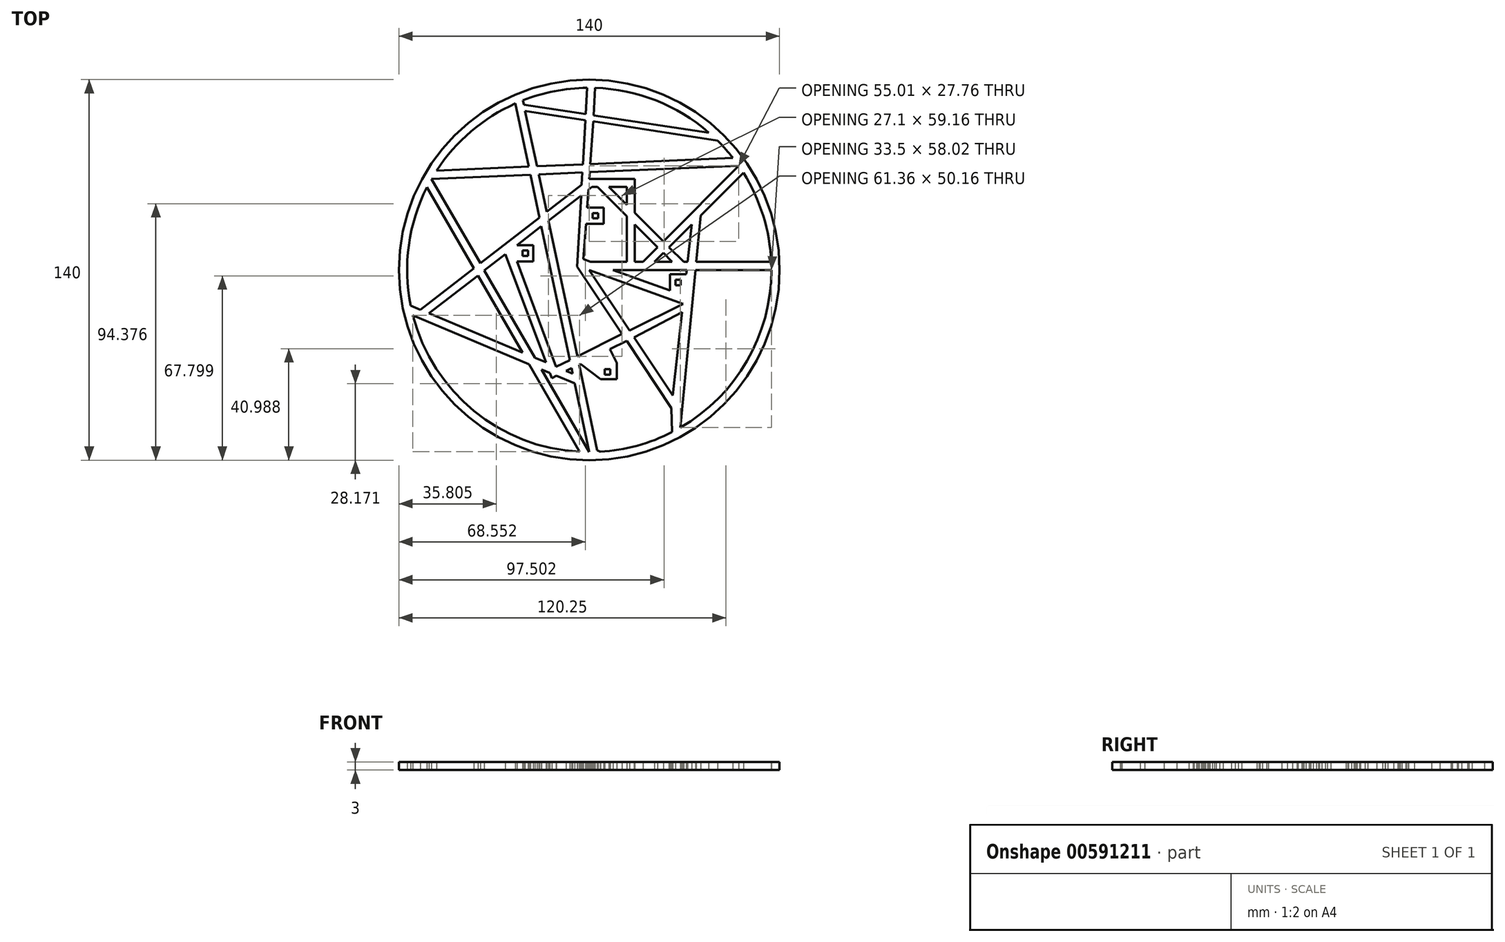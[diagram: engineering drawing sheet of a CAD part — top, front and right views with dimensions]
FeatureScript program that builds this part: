
annotation { "Feature Type Name" : "Feature", "Feature Type Description" : "" }
export const myFeature = defineFeature(function(context is Context, id is Id, definition is map)
    precondition{}
    {
        {
            var Q0;
            Q0=qCreatedBy(makeId("Top.planeOp"),FACE);
            var sketch = newSketch(context, id + "F0", { "sketchPlane" : qUnion([Q0])});
            skCircle(sketch, "E0", {"center": v(0, 0) * mm, "radius": 70 * mm});
            skArc(sketch, "E1.0", {"start": v(66.93, 3) * mm, "mid": v(63.94, 20.02) * mm, "end": v(56.7, 35.7) * mm});
            skLineSegment(sketch, "E2", {"start": v(67, 0) * mm, "end": v(39.1, 0) * mm});
            skLineSegment(sketch, "E3", {"start": v(30.5, 3) * mm, "end": v(27.25, 6.25) * mm});
            skLineSegment(sketch, "E4", {"start": v(0, 33.5) * mm, "end": v(16.75, 33.5) * mm});
            skPoint(sketch, "E4.endSnap0", {"position": v(16.75, 16.75) * mm});
            skLineSegment(sketch, "E5", {"start": v(16.75, 33.5) * mm, "end": v(16.75, 21) * mm});
            skLineSegment(sketch, "E6", {"start": v(19.75, 3) * mm, "end": v(25.12, 8.37) * mm});
            skLineSegment(sketch, "E7", {"start": v(55, 38.26) * mm, "end": v(0.18, 35.95) * mm});
            skPoint(sketch, "E7.endSnap0", {"position": v(8.38, 33.5) * mm});
            skLineSegment(sketch, "E8", {"start": v(-58.02, 33.5) * mm, "end": v(-40.1, 2.44) * mm});
            skLineSegment(sketch, "E9", {"start": v(0, -67) * mm, "end": v(-5.37, -41.72) * mm});
            skLineSegment(sketch, "E10", {"start": v(-24.05, 60.75) * mm, "end": v(-1.35, 57.34) * mm});
            skPoint(sketch, "E11.endSnap0", {"position": v(-29.01, -16.75) * mm});
            skLineSegment(sketch, "E12", {"start": v(-62.15, -14.64) * mm, "end": v(-42.49, 0.59) * mm});
            skLineSegment(sketch, "E13.0", {"start": v(-58.97, -15.97) * mm, "end": v(-40.97, -2.03) * mm});
            skLineSegment(sketch, "E14.0", {"start": v(67, 3) * mm, "end": v(39.39, 3) * mm});
            skLineSegment(sketch, "E15.0", {"start": v(-0.82, 67) * mm, "end": v(-1.35, 57.34) * mm});
            skLineSegment(sketch, "E16.0", {"start": v(52.86, 41.17) * mm, "end": v(0.4, 38.96) * mm});
            skLineSegment(sketch, "E16.1", {"start": v(24, 3) * mm, "end": v(27.25, 6.25) * mm});
            skLineSegment(sketch, "E17.0", {"start": v(13.75, 30.5) * mm, "end": v(13.75, 24) * mm});
            skLineSegment(sketch, "E17.1", {"start": v(1.03, 30.5) * mm, "end": v(3, 30.5) * mm});
            skLineSegment(sketch, "E18.0", {"start": v(34.74, 3) * mm, "end": v(29.37, 8.37) * mm});
            skLineSegment(sketch, "E19", {"start": v(-26.63, 3.13) * mm, "end": v(-12.15, -35.62) * mm});
            skLineSegment(sketch, "E20", {"start": v(-12.15, -35.62) * mm, "end": v(-7.19, -33.15) * mm});
            skLineSegment(sketch, "E21", {"start": v(34.46, -12.53) * mm, "end": v(0, 0) * mm});
            skLineSegment(sketch, "E22", {"start": v(30.23, -50.85) * mm, "end": v(13.76, -26.1) * mm});
            skLineSegment(sketch, "E23.0", {"start": v(30.74, -46.2) * mm, "end": v(16.47, -24.76) * mm});
            skLineSegment(sketch, "E24.0", {"start": v(-13.8, -39.78) * mm, "end": v(-12.05, -38.91) * mm});
            skLineSegment(sketch, "E24.1", {"start": v(-30.84, 5.82) * mm, "end": v(-15.95, -34.02) * mm});
            skLineSegment(sketch, "E25.0", {"start": v(29.67, -7.6) * mm, "end": v(8.78, 0) * mm});
            skLineSegment(sketch, "E26.0", {"start": v(-59.7, 30.4) * mm, "end": v(-42.49, 0.59) * mm});
            skLineSegment(sketch, "E27.0", {"start": v(2.93, -66.38) * mm, "end": v(-3.76, -34.86) * mm});
            skLineSegment(sketch, "E28", {"start": v(2.93, -66.38) * mm, "end": v(3.98, -66.88) * mm});
            skLineSegment(sketch, "E29.trimOffspring", {"start": v(0.53, 3) * mm, "end": v(-2.13, 3.97) * mm});
            skLineSegment(sketch, "E30.trimOffspring", {"start": v(13.75, 3) * mm, "end": v(0.53, 3) * mm});
            skPoint(sketch, "E31.orphan", {"position": v(16.75, 0) * mm});
            skLineSegment(sketch, "E32.trimOffspring", {"start": v(19.75, 3) * mm, "end": v(16.75, 3) * mm});
            skPoint(sketch, "E33.orphan", {"position": v(33.5, 0) * mm});
            skLineSegment(sketch, "E34.trimOffspring", {"start": v(30.5, 3) * mm, "end": v(24, 3) * mm});
            skLineSegment(sketch, "E35.trimOffspring", {"start": v(29.37, 8.37) * mm, "end": v(37.7, 16.7) * mm});
            skLineSegment(sketch, "E36.trimOffspring", {"start": v(27.25, 10.5) * mm, "end": v(16.75, 21) * mm});
            skLineSegment(sketch, "E37.trimOffspring", {"start": v(27.25, 10.5) * mm, "end": v(55, 38.26) * mm});
            skLineSegment(sketch, "E38.trimOffspring", {"start": v(25.12, 8.38) * mm, "end": v(16.75, 16.75) * mm});
            skLineSegment(sketch, "E39.trimOffspring", {"start": v(37.7, 16.7) * mm, "end": v(36.18, 3) * mm});
            skLineSegment(sketch, "E40.trimOffspring", {"start": v(41.03, 20.04) * mm, "end": v(39.39, 3) * mm});
            skLineSegment(sketch, "E41.trimOffspring", {"start": v(-5.37, -41.72) * mm, "end": v(-12.05, -38.91) * mm});
            skPoint(sketch, "E42.0.start.orphan", {"position": v(39.06, 29.09) * mm});
            skLineSegment(sketch, "E43.trimOffspring", {"start": v(41.03, 20.04) * mm, "end": v(56.7, 35.7) * mm});
            skLineSegment(sketch, "E44.trimOffspring", {"start": v(35.85, 0) * mm, "end": v(8.78, 0) * mm});
            skLineSegment(sketch, "E45.trimOffspring", {"start": v(35.85, 0) * mm, "end": v(35.67, -1.6) * mm});
            skLineSegment(sketch, "E46.trimOffspring", {"start": v(36.18, 3) * mm, "end": v(34.74, 3) * mm});
            skLineSegment(sketch, "E47.trimOffspring", {"start": v(39.1, 0) * mm, "end": v(33.5, -58.02) * mm});
            skPoint(sketch, "E13.1.start.orphan", {"position": v(34.66, -55.26) * mm});
            skArc(sketch, "E48.trimOffspring", {"start": v(3.98, -66.88) * mm, "mid": v(17.62, -64.64) * mm, "end": v(30.5, -59.66) * mm});
            skLineSegment(sketch, "E49.trimOffspring", {"start": v(-6.13, -38.14) * mm, "end": v(-8.5, -37.15) * mm});
            skLineSegment(sketch, "E50.trimOffspring", {"start": v(-6.13, -38.14) * mm, "end": v(-6.54, -36.18) * mm});
            skLineSegment(sketch, "E51.trimOffspring", {"start": v(16.47, -24.76) * mm, "end": v(34.13, -15.53) * mm});
            skLineSegment(sketch, "E52.trimOffspring", {"start": v(14.81, -22.26) * mm, "end": v(34.46, -12.53) * mm});
            skLineSegment(sketch, "E53.trimOffspring", {"start": v(14.81, -22.26) * mm, "end": v(0, 0) * mm});
            skLineSegment(sketch, "E54.trimOffspring", {"start": v(12.1, -23.6) * mm, "end": v(-4.44, 1.26) * mm});
            skLineSegment(sketch, "E55.trimOffspring", {"start": v(-4.4, -31.78) * mm, "end": v(-15, 18.09) * mm});
            skLineSegment(sketch, "E56.trimOffspring", {"start": v(-7.19, -33.15) * mm, "end": v(-17.63, 16.05) * mm});
            skLineSegment(sketch, "E57.trimOffspring", {"start": v(-4.4, -31.78) * mm, "end": v(12.1, -23.6) * mm});
            skLineSegment(sketch, "E58.trimOffspring", {"start": v(-8.5, -37.15) * mm, "end": v(-6.54, -36.18) * mm});
            skLineSegment(sketch, "E59.trimOffspring", {"start": v(-15.95, -34.02) * mm, "end": v(-20.03, -32.31) * mm});
            skLineSegment(sketch, "E60.trimOffspring", {"start": v(-14.51, -37.88) * mm, "end": v(-17.55, -36.6) * mm});
            skLineSegment(sketch, "E61.trimOffspring", {"start": v(-14.51, -37.88) * mm, "end": v(-13.8, -39.78) * mm});
            skLineSegment(sketch, "E62.trimOffspring", {"start": v(-17.55, -36.6) * mm, "end": v(0, -67) * mm});
            skLineSegment(sketch, "E63.trimOffspring", {"start": v(-22.12, -34.69) * mm, "end": v(-3.52, -66.9) * mm});
            skLineSegment(sketch, "E64.trimOffspring", {"start": v(-22.12, -34.69) * mm, "end": v(-64.87, -16.75) * mm});
            skLineSegment(sketch, "E65.trimOffspring", {"start": v(-24.6, -30.4) * mm, "end": v(-58.97, -15.97) * mm});
            skArc(sketch, "E66.trimOffspring", {"start": v(-59.7, 30.4) * mm, "mid": v(-66.37, 9.13) * mm, "end": v(-65.7, -13.15) * mm});
            skLineSegment(sketch, "E67.trimOffspring", {"start": v(-23.58, 58.54) * mm, "end": v(-1.48, 55.11) * mm});
            skArc(sketch, "E68.trimOffspring", {"start": v(-27.22, 61.22) * mm, "mid": v(-43.46, 51) * mm, "end": v(-56.13, 36.58) * mm});
            skLineSegment(sketch, "E69.trimOffspring", {"start": v(-24.05, 60.75) * mm, "end": v(-24.4, 62.4) * mm});
            skLineSegment(sketch, "E70.trimOffspring", {"start": v(-1.48, 55.11) * mm, "end": v(-2.37, 38.84) * mm});
            skLineSegment(sketch, "E71.trimOffspring", {"start": v(1.65, 56.9) * mm, "end": v(43.97, 50.55) * mm});
            skLineSegment(sketch, "E72.trimOffspring", {"start": v(1.52, 54.64) * mm, "end": v(47.2, 47.55) * mm});
            skLineSegment(sketch, "E73.trimOffspring", {"start": v(1.52, 54.64) * mm, "end": v(0.4, 38.96) * mm});
            skPoint(sketch, "E74.start.orphan", {"position": v(0, 67) * mm});
            skLineSegment(sketch, "E75.trimOffspring", {"start": v(-2.37, 38.84) * mm, "end": v(-19.25, 38.13) * mm});
            skLineSegment(sketch, "E76.trimOffspring", {"start": v(0.18, 35.95) * mm, "end": v(0, 33.5) * mm});
            skLineSegment(sketch, "E77.trimOffspring", {"start": v(-2.54, 35.83) * mm, "end": v(-18.62, 35.16) * mm});
            skLineSegment(sketch, "E78.trimOffspring", {"start": v(-2.54, 35.83) * mm, "end": v(-2.78, 31.34) * mm});
            skLineSegment(sketch, "E79.trimOffspring", {"start": v(-22.3, 38) * mm, "end": v(-56.13, 36.58) * mm});
            skLineSegment(sketch, "E80.trimOffspring", {"start": v(-22.3, 38) * mm, "end": v(-27.22, 61.22) * mm});
            skLineSegment(sketch, "E81.trimOffspring", {"start": v(-19.25, 38.13) * mm, "end": v(-23.58, 58.54) * mm});
            skLineSegment(sketch, "E82.trimOffspring", {"start": v(-21.66, 35.03) * mm, "end": v(-58.02, 33.5) * mm});
            skLineSegment(sketch, "E83.trimOffspring", {"start": v(-15.69, 21.35) * mm, "end": v(-2.78, 31.34) * mm});
            skLineSegment(sketch, "E84.trimOffspring", {"start": v(-15.69, 21.35) * mm, "end": v(-18.62, 35.16) * mm});
            skLineSegment(sketch, "E85.trimOffspring", {"start": v(-15, 18.09) * mm, "end": v(-3, 27.38) * mm});
            skLineSegment(sketch, "E86.trimOffspring", {"start": v(-18.32, 19.3) * mm, "end": v(-21.66, 35.03) * mm});
            skLineSegment(sketch, "E87.trimOffspring", {"start": v(-26.56, 9.13) * mm, "end": v(-17.63, 16.05) * mm});
            skLineSegment(sketch, "E88.trimOffspring", {"start": v(-38.58, -0.18) * mm, "end": v(-20.03, -32.31) * mm});
            skLineSegment(sketch, "E89.trimOffspring", {"start": v(-40.1, 2.44) * mm, "end": v(-18.32, 19.3) * mm});
            skLineSegment(sketch, "E90.trimOffspring", {"start": v(-40.97, -2.03) * mm, "end": v(-24.6, -30.4) * mm});
            skLineSegment(sketch, "E91.trimOffspring", {"start": v(-38.58, -0.18) * mm, "end": v(-30.84, 5.82) * mm});
            skLineSegment(sketch, "E92.trimOffspring", {"start": v(34.13, -15.53) * mm, "end": v(30.74, -46.2) * mm});
            skLineSegment(sketch, "E93.trimOffspring", {"start": v(13.75, 24) * mm, "end": v(7.24, 30.5) * mm});
            skLineSegment(sketch, "E94.trimOffspring", {"start": v(13.75, 19.75) * mm, "end": v(13.75, 3) * mm});
            skLineSegment(sketch, "E95.trimOffspring", {"start": v(13.75, 19.75) * mm, "end": v(3, 30.5) * mm});
            skLineSegment(sketch, "E96.trimOffspring", {"start": v(16.75, 16.75) * mm, "end": v(16.75, 3) * mm});
            skLineSegment(sketch, "E97.trimOffspring", {"start": v(7.24, 30.5) * mm, "end": v(13.75, 30.5) * mm});
            skPoint(sketch, "E98.trimOffspring.end.orphan", {"position": v(2.27, 31.46) * mm});
            skLineSegment(sketch, "E99.trimOffspring", {"start": v(-0.29, 29.48) * mm, "end": v(-0.76, 22.96) * mm});
            skLineSegment(sketch, "E100.trimOffspring", {"start": v(-0.29, 29.48) * mm, "end": v(1.03, 30.5) * mm});
            skLineSegment(sketch, "E101.trimOffspring", {"start": v(-3, 27.38) * mm, "end": v(-4.44, 1.26) * mm});
            skArc(sketch, "E102.trimOffspring", {"start": v(43.97, 50.55) * mm, "mid": v(24.5, 62.36) * mm, "end": v(2.18, 66.96) * mm});
            skArc(sketch, "E103.trimOffspring", {"start": v(52.86, 41.17) * mm, "mid": v(50.13, 44.45) * mm, "end": v(47.2, 47.55) * mm});
            skLineSegment(sketch, "E104", {"start": v(1.65, 56.9) * mm, "end": v(2.18, 66.96) * mm});
            skArc(sketch, "E105.trimOffspring", {"start": v(-0.82, 67) * mm, "mid": v(-12.82, 65.76) * mm, "end": v(-24.4, 62.4) * mm});
            skLineSegment(sketch, "E106.bottom", {"start": v(-0.76, 22.96) * mm, "end": v(5.24, 22.96) * mm});
            skLineSegment(sketch, "E106.top", {"start": v(-1.2, 16.96) * mm, "end": v(5.24, 16.96) * mm});
            skLineSegment(sketch, "E106.right", {"start": v(5.24, 22.96) * mm, "end": v(5.24, 16.96) * mm});
            skLineSegment(sketch, "E107.0", {"start": v(1.24, 20.96) * mm, "end": v(3.24, 20.96) * mm});
            skLineSegment(sketch, "E107.1", {"start": v(1.24, 20.96) * mm, "end": v(1.24, 18.96) * mm});
            skLineSegment(sketch, "E107.2", {"start": v(1.24, 18.96) * mm, "end": v(3.24, 18.96) * mm});
            skLineSegment(sketch, "E107.3", {"start": v(3.24, 20.96) * mm, "end": v(3.24, 18.96) * mm});
            skLineSegment(sketch, "E108.trimOffspring", {"start": v(-1.2, 16.96) * mm, "end": v(-2.13, 3.97) * mm});
            skLineSegment(sketch, "E109", {"start": v(-3.76, -34.86) * mm, "end": v(-3.27, -34.61) * mm});
            skLineSegment(sketch, "E110.top", {"start": v(4.12, -40.25) * mm, "end": v(10.12, -40.25) * mm});
            skLineSegment(sketch, "E110.right", {"start": v(10.12, -34.25) * mm, "end": v(10.12, -40.25) * mm});
            skLineSegment(sketch, "E111.0", {"start": v(5.66, -38.52) * mm, "end": v(7.66, -38.52) * mm});
            skLineSegment(sketch, "E111.1", {"start": v(7.66, -36.52) * mm, "end": v(7.66, -38.52) * mm});
            skLineSegment(sketch, "E111.2", {"start": v(5.66, -36.52) * mm, "end": v(7.66, -36.52) * mm});
            skLineSegment(sketch, "E112.0", {"start": v(5.66, -36.52) * mm, "end": v(5.66, -38.52) * mm});
            skLineSegment(sketch, "E113", {"start": v(4.12, -40.25) * mm, "end": v(-3.28, -34.6) * mm});
            skLineSegment(sketch, "E114", {"start": v(10.12, -34.25) * mm, "end": v(7.6, -29.19) * mm});
            skLineSegment(sketch, "E115.trimOffspring", {"start": v(7.6, -29.19) * mm, "end": v(13.76, -26.1) * mm});
            skLineSegment(sketch, "E116.bottom", {"start": v(-26.56, 9.13) * mm, "end": v(-20.56, 9.13) * mm});
            skLineSegment(sketch, "E116.top", {"start": v(-26.63, 3.13) * mm, "end": v(-20.56, 3.13) * mm});
            skLineSegment(sketch, "E116.right", {"start": v(-20.56, 9.13) * mm, "end": v(-20.56, 3.13) * mm});
            skLineSegment(sketch, "E117.0", {"start": v(-24.56, 7.13) * mm, "end": v(-22.56, 7.13) * mm});
            skLineSegment(sketch, "E117.1", {"start": v(-24.56, 7.13) * mm, "end": v(-24.56, 5.13) * mm});
            skLineSegment(sketch, "E117.2", {"start": v(-24.56, 5.13) * mm, "end": v(-22.56, 5.13) * mm});
            skLineSegment(sketch, "E117.3", {"start": v(-22.56, 7.13) * mm, "end": v(-22.56, 5.13) * mm});
            skPoint(sketch, "E118.orphan", {"position": v(-28.35, 7.74) * mm});
            skLineSegment(sketch, "E119.top", {"start": v(29.67, -1.6) * mm, "end": v(35.67, -1.6) * mm});
            skLineSegment(sketch, "E119.left", {"start": v(29.67, -7.6) * mm, "end": v(29.67, -1.6) * mm});
            skLineSegment(sketch, "E120.0", {"start": v(33.67, -5.6) * mm, "end": v(33.67, -3.6) * mm});
            skLineSegment(sketch, "E120.1", {"start": v(31.67, -3.6) * mm, "end": v(33.67, -3.6) * mm});
            skLineSegment(sketch, "E120.2", {"start": v(31.67, -5.6) * mm, "end": v(31.67, -3.6) * mm});
            skLineSegment(sketch, "E121.0", {"start": v(31.67, -5.6) * mm, "end": v(33.67, -5.6) * mm});
            skLineSegment(sketch, "E122", {"start": v(30.23, -50.85) * mm, "end": v(30.5, -59.66) * mm});
            skPoint(sketch, "E123.trimOffspring.end.orphan", {"position": v(29.86, -54.16) * mm});
            skArc(sketch, "E124.trimOffspring", {"start": v(33.5, -58.02) * mm, "mid": v(58.02, -33.5) * mm, "end": v(67, 0) * mm});
            skLineSegment(sketch, "E125", {"start": v(-62.15, -14.64) * mm, "end": v(-65.7, -13.15) * mm});
            skArc(sketch, "E126.trimOffspring", {"start": v(-64.87, -16.75) * mm, "mid": v(-42.4, -51.87) * mm, "end": v(-3.52, -66.9) * mm});
            skSolve(sketch);
        }
        {
            var Q0;
            Q0=makeQuery(id+"F0.imprint","IMPRINT",FACE,{"disambiguationData":[TD([[makeQuery(id+"F0.imprint","IMPRINT",EDGE,{"derivedFrom":sQuery(id+"F0.wireOp",EDGE,"E0")}),1.0]])]});
            extrude(context, id + "F1", {"entities" : qUnion([Q0]), "depth" : 3 * mm, "offsetDistance" : 25 * mm});
        }
    });
